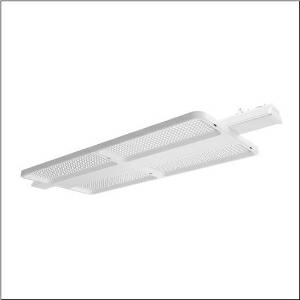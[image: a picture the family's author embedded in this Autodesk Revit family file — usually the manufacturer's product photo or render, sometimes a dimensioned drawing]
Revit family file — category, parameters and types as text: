
# Revit family: highbay_11_fur_licross_r__tragschiene_maxi_51hn12db4qla_55c1
name_source: partatom
category: Lighting Fixtures
units: mm (PartAtom-declared; Revit-internal decimal feet)

## family parameters
Cut with Voids When Loaded = No
Host = Face
Light Source = No
Part Type = Normal
Room Calculation Point = No
Round Connector Dimension = Use Diameter
Shared = No

## types (1)
- --- (1 x LED, 36000 lm, 177.7 W, 4000K)
    Apparent Load = 178 VA
    CIE Flux Codes = 87 98 100 100 100
    Color Rendering = 80
    Color Temperature = 4000K
    Default Elevation = 1800 mm
    Description = Highbay 11 for Licross® trunking rail maxi, high bay luminaire, primary light control with lens, of PMMA, primary optical cover: cover, of PMMA, light emission: direct distribution, primary light characteristic: symmetric, LED, rated luminous flux: 36.000lm, luminous efficacy: 203lm/W, light colour: 840, colour temperature: 4000K, control gear: DALI 2, with plug, 5-pole, with phase selection, mains connection: 230..240V, AC, 50/60Hz, rated input power: 177.7W, housing frame, of high-performance plastic PA6, matt traffic white (RAL 9016), length: 1.250mm, width: 442mm, height: 71mm, lever catch, fixing on rail side, of steel, galvanised, white, blank cover, of PC/ABS, traffic white (RAL 9016), protection rating (complete): IP64, insulation class (complete): insulation class I (protective earthing), certification: CE, ENEC, VDE, UKCA, protection symbol: D, impact resistance: IK07, permissible operating ambient temperature: -40..+55°C, corresponds to IFS (International Featured Standards) requirements for safety and quality in the food industry, LABS conformity tested according to VDMA 24364:2018-05, packaging unit: 1 piece
    Height = 72 mm  [stored 0.23622 ft]
    Lamp = 1 x LED
    Lamp Light Flux = 36000 lm
    Lamp Power = 177.7 W
    Lamp count = 1
    Length = 946 mm
    Luminous efficacy = 203 lm/W
    Manufacturer = Siteco
    ModVariant = No
    Model = 51HN12DB4QLA
    Mounting Place = Ceiling
    Mounting Type = Pendant
    Number of Poles = 1
    OnlyDefault = Yes
    Power Factor = 1
    Product Name = Highbay 11 für Licross® Tragschiene maxi
    Product group = high bay luminaire
    ProductGroupID = 901
    Protection Class = Protection class I
    Protection Degree = IP 64
    RLX_Detail_Level = 1
    RLX_Emergency_Light_Flux = 0 lm
    RLX_Emergency_Type = 0
    RLX_Emergency_Type_DB = No
    RlxData = <blob elided: 24045 chars, md5=3b18e8dd>
    Socket = socket
    Standby Power = 0 W
    System Light Flux = 36000 lm
    System Power = 178 W
    Type Comments = factory setting: luminous flux: 100 % | dim-lin: 254 | 824 mA
    Type Image = l_1361711.jpg
    URL = http://relux.com
    VarID = @adj_006365
    Voltage = 0 V
    Weight = 0.00 kg
    Width = 442 mm

note: [stored X ft] marks values corroborated as IEEE doubles in the binary element streams (Revit-internal decimal feet)

## geometry (parser evidence)
native form markers: Blend x4, Sweep x12
no freeform markers — native parametric forms only
